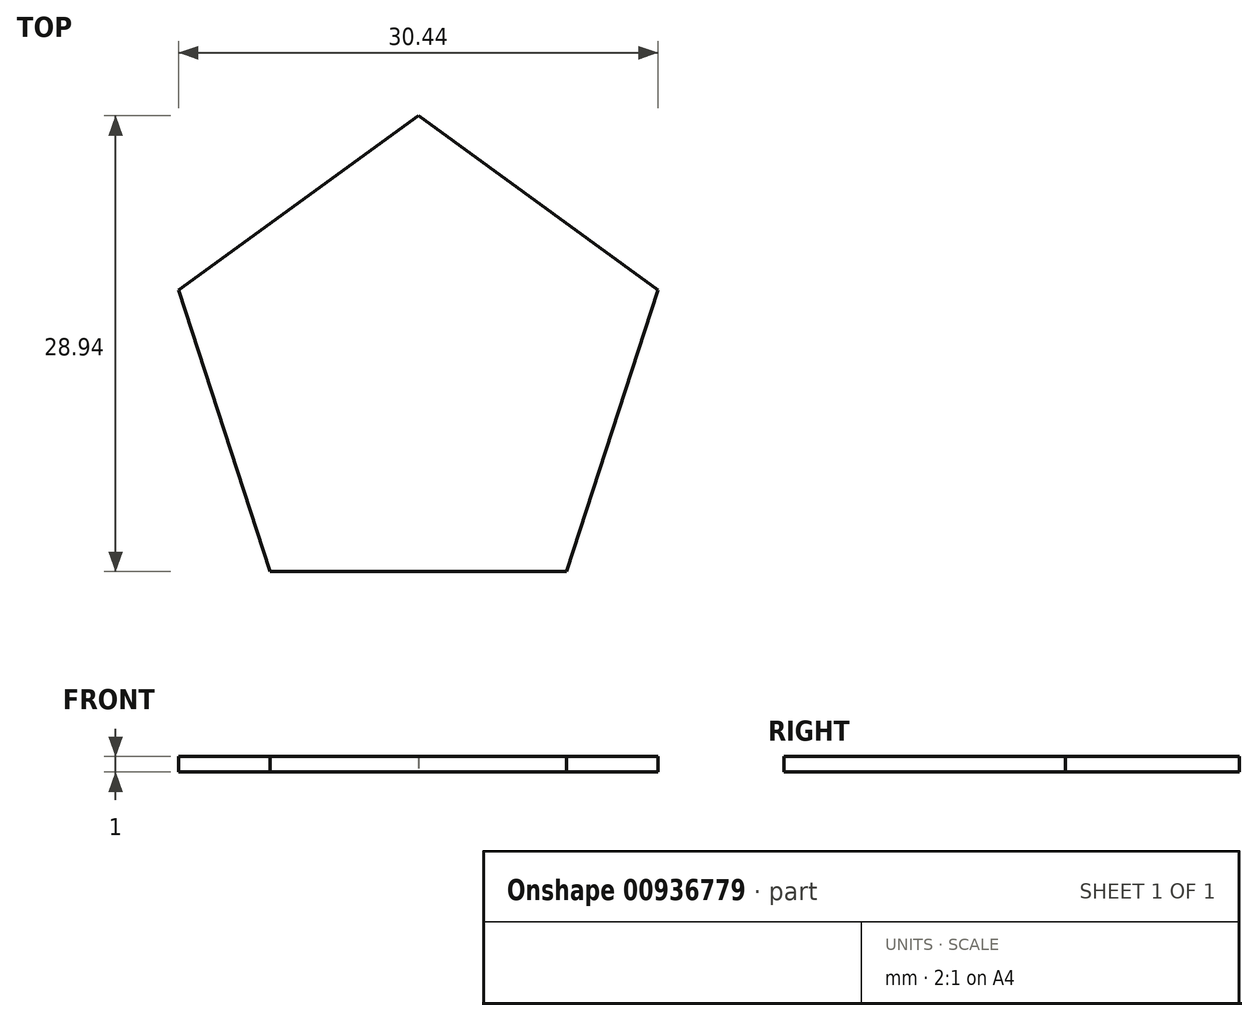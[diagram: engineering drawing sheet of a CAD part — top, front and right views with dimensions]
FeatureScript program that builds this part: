
annotation { "Feature Type Name" : "Feature", "Feature Type Description" : "" }
export const myFeature = defineFeature(function(context is Context, id is Id, definition is map)
    precondition{}
    {
        {
            var Q0;
            Q0=qCreatedBy(makeId("Top.planeOp"),FACE);
            var sketch = newSketch(context, id + "F0", { "sketchPlane" : qUnion([Q0])});
            skCircle(sketch, "E0.cCircle", {"center": v(0, 0) * mm, "radius": 16 * mm, "construction": true});
            skLineSegment(sketch, "E0.0", {"start": v(-9.4, -12.94) * mm, "end": v(-15.22, 4.94) * mm});
            skLineSegment(sketch, "E0.1", {"start": v(-15.22, 4.94) * mm, "end": v(0, 16) * mm});
            skLineSegment(sketch, "E0.2", {"start": v(0, 16) * mm, "end": v(15.22, 4.94) * mm});
            skLineSegment(sketch, "E0.3", {"start": v(15.22, 4.94) * mm, "end": v(9.4, -12.94) * mm});
            skLineSegment(sketch, "E0.4", {"start": v(9.4, -12.94) * mm, "end": v(-9.4, -12.94) * mm});
            skSolve(sketch);
        }
        {
            var Q0;
            Q0 = qSketchRegion(id + "F0", true);
            extrude(context, id + "F1", {"entities" : qUnion([Q0]), "depth" : 1 * mm, "offsetDistance" : 25 * mm});
        }
    });
